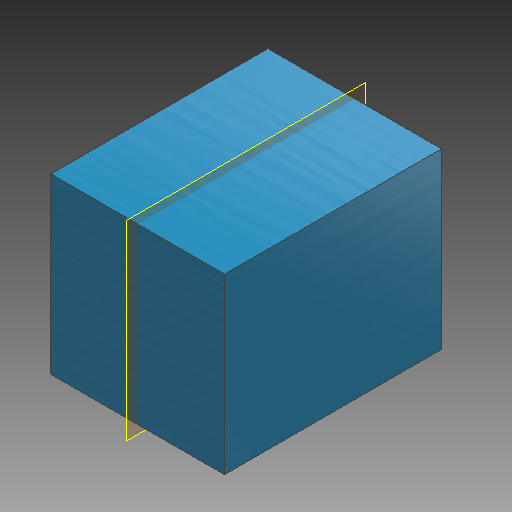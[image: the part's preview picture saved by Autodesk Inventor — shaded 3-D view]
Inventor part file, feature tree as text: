
AUTODESK INVENTOR PART (.ipt)
format: ipt  version: 2017 (Build 210142000, 142)  size: 156,672 bytes
history: native  units: mm
features: reference x20, other x3, sketch x2, extrude x1, plane x1, revolve x1, projected_geometry x1
ambient origin geometry x8: Origin, YZ Plane, XZ Plane, XY Plane, X Axis, Y Axis, Z Axis, Center Point
bodies: Solid1 (feature_tree)
feature tree (29):
  extrude  "Extrusion1"  Depth=160.0mm TaperAngle=0.0deg
  plane  "Work Plane1"
  revolve  "Revolution1"  [1 undecoded]
  sketch  "Sketch1"  dims[d0=160.0mm d1=160.0mm d2=0.0mm]
  reference  "Reference1"
  reference  "Reference2"
  reference  "Reference3"
  reference  "Reference4"
  reference  "Reference5"
  reference  "Reference6"
  reference  "Reference7"
  reference  "Reference8"
  reference  "Reference9"
  reference  "Reference10"
  reference  "Reference11"
  reference  "Reference12"
  reference  "Reference13"
  reference  "Reference14"
  reference  "Reference15"
  reference  "Reference16"
  reference  "Reference17"
  reference  "Reference18"
  reference  "Reference19"
  reference  "Reference20"
  sketch  "Sketch2"  dims[d6=8.0mm d7=12.0mm d8=20.0mm d9=30.0mm d10=94.989305mm d11=90.0deg]
  projected_geometry  "Projected Loop1"
  other  "<userpath>\OneDrive\Inventor\VolledigGeassembleerdv001.iam"
  other  "VolledigGeassembleerdv001.iam"
  other  "Frame:1"
note: 1 required parameter value undecoded (feature->parameter linkage not recoverable at this tier; creation-order binding heuristic only, values carry confidence <= 0.55)
